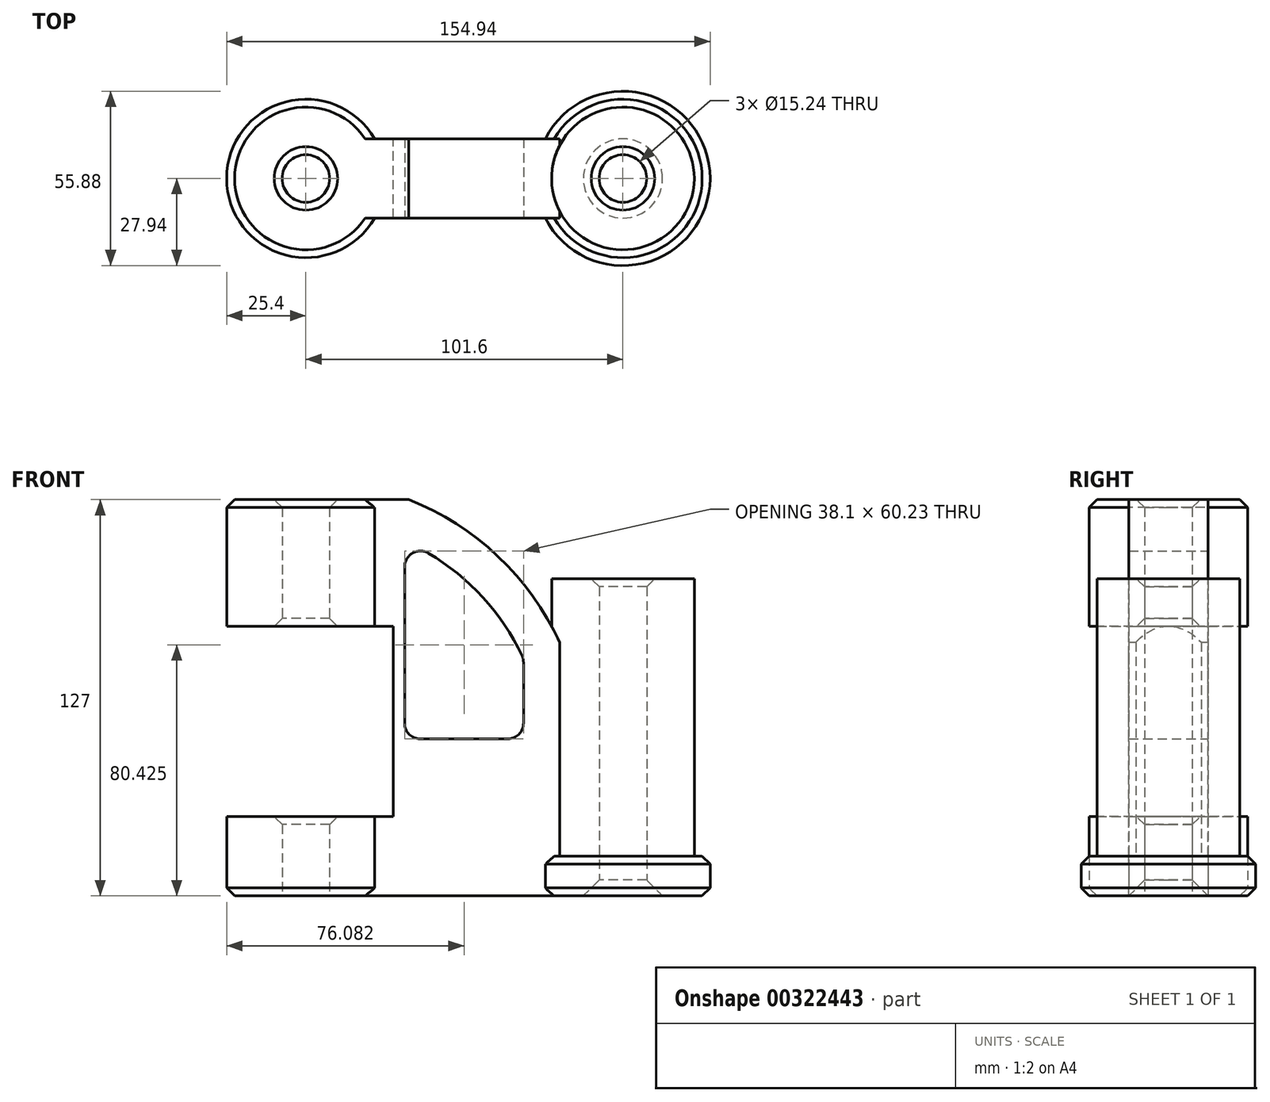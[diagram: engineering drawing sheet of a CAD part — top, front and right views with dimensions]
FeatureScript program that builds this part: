
annotation { "Feature Type Name" : "Feature", "Feature Type Description" : "" }
export const myFeature = defineFeature(function(context is Context, id is Id, definition is map)
    precondition{}
    {
        {
            var Q0;
            Q0=qCreatedBy(makeId("Top.planeOp"),FACE);
            var sketch = newSketch(context, id + "F0", { "sketchPlane" : qUnion([Q0])});
            skCircle(sketch, "E0", {"center": v(0, 0) * mm, "radius": 7.62 * mm});
            skCircle(sketch, "E1", {"center": v(0, 0) * mm, "radius": 25.4 * mm});
            skCircle(sketch, "E2", {"center": v(101.6, 0) * mm, "radius": 7.62 * mm});
            skCircle(sketch, "E3", {"center": v(101.6, 0) * mm, "radius": 22.86 * mm});
            skSolve(sketch);
        }
        {
            var Q0;
            Q0=makeQuery(id+"F0.imprint","IMPRINT",FACE,{"disambiguationData":[TD([[makeQuery(id+"F0.imprint","IMPRINT",EDGE,{"derivedFrom":sQuery(id+"F0.wireOp",EDGE,"E0")}),-1.0]])]});
            extrude(context, id + "F1", {"entities" : qUnion([Q0]), "depth" : 127 * mm});
        }
        {
            var Q0;
            Q0=makeQuery(id+"F0.imprint","IMPRINT",FACE,{"disambiguationData":[TD([[makeQuery(id+"F0.imprint","IMPRINT",EDGE,{"derivedFrom":sQuery(id+"F0.wireOp",EDGE,"E2")}),-1.0]])]});
            extrude(context, id + "F2", {"entities" : qUnion([Q0]), "depth" : 101.6 * mm});
        }
        {
            var Q0;
            Q0=qCreatedBy(makeId("Front.planeOp"),FACE);
            var sketch = newSketch(context, id + "F3", { "sketchPlane" : qUnion([Q0])});
            skLineSegment(sketch, "E4", {"start": v(20.32, 0) * mm, "end": v(20.32, 127) * mm});
            skLineSegment(sketch, "E5", {"start": v(20.32, 127) * mm, "end": v(33.02, 127) * mm});
            skLineSegment(sketch, "E6", {"start": v(20.32, 0) * mm, "end": v(81.28, 0) * mm});
            skLineSegment(sketch, "E7", {"start": v(81.28, 0) * mm, "end": v(81.28, 81.28) * mm});
            skArc(sketch, "E8", {"start": v(81.28, 81.28) * mm, "mid": v(61.58, 108.82) * mm, "end": v(33.02, 127) * mm});
            skArc(sketch, "E9.0", {"start": v(69.73, 76) * mm, "mid": v(54.12, 98.37) * mm, "end": v(31.63, 113.8) * mm});
            skLineSegment(sketch, "E10", {"start": v(31.63, 113.8) * mm, "end": v(31.63, 50.3) * mm});
            skLineSegment(sketch, "E11", {"start": v(31.63, 50.3) * mm, "end": v(69.73, 50.3) * mm});
            skLineSegment(sketch, "E12", {"start": v(69.73, 50.3) * mm, "end": v(69.73, 76) * mm});
            skSolve(sketch);
        }
        {
            var Q0;
            Q0 = qSketchRegion(id + "F3", true);
            extrude(context, id + "F4", {"entities" : qUnion([Q0]), "operationType" : NewBodyOperationType.ADD, "depth" : 25.4 * mm, "symmetric" : true});
        }
        {
            var Q0;
            Q0=qCreatedBy(makeId("Front.planeOp"),FACE);
            var sketch = newSketch(context, id + "F5", { "sketchPlane" : qUnion([Q0])});
            skLineSegment(sketch, "E13.bottom", {"start": v(-33.02, 25.4) * mm, "end": v(27.94, 25.4) * mm});
            skLineSegment(sketch, "E13.top", {"start": v(-33.02, 86.36) * mm, "end": v(27.94, 86.36) * mm});
            skLineSegment(sketch, "E13.left", {"start": v(-33.02, 25.4) * mm, "end": v(-33.02, 86.36) * mm});
            skLineSegment(sketch, "E13.right", {"start": v(27.94, 25.4) * mm, "end": v(27.94, 86.36) * mm});
            skSolve(sketch);
        }
        {
            var Q0;
            Q0 = qSketchRegion(id + "F5", true);
            extrude(context, id + "F6", {"entities" : qUnion([Q0]), "operationType" : NewBodyOperationType.REMOVE, "depth" : 101.6 * mm, "symmetric" : true});
        }
        {
            var Q0;
            Q0=makeQuery(id+"F4.opExtrude","SWEPT_EDGE",EDGE,{"disambiguationData":[OSD([sQuery(id+"F3.wireOp",EDGE,"E10"),sQuery(id+"F3.wireOp",EDGE,"E11")])]});
            var Q1;
            Q1=makeQuery(id+"F4.opExtrude","SWEPT_EDGE",EDGE,{"disambiguationData":[OSD([sQuery(id+"F3.wireOp",EDGE,"E9.0"),sQuery(id+"F3.wireOp",EDGE,"E10")])]});
            var Q2;
            Q2=makeQuery(id+"F4.opExtrude","SWEPT_EDGE",EDGE,{"disambiguationData":[OSD([sQuery(id+"F3.wireOp",EDGE,"E11"),sQuery(id+"F3.wireOp",EDGE,"E12")])]});
            var Q3;
            Q3=makeQuery(id+"F4.opExtrude","SWEPT_EDGE",EDGE,{"disambiguationData":[OSD([sQuery(id+"F3.wireOp",EDGE,"E9.0"),sQuery(id+"F3.wireOp",EDGE,"E12")])]});
            fillet(context, id + "F7", {"entities" : qUnion([Q0, Q1, Q2, Q3]), "radius" : 5.08 * mm, "tangentPropagation" : true, "allowEdgeOverflow" : false});
        }
        {
            var Q0;
            Q0=makeQuery(id+"F1.opExtrude","CAP_EDGE",EDGE,{"disambiguationData":[OSD([sQuery(id+"F0.wireOp",EDGE,"E1")])],"isStart":false});
            var Q1;
            Q1=makeQuery(id+"F1.opExtrude","CAP_EDGE",EDGE,{"disambiguationData":[OSD([sQuery(id+"F0.wireOp",EDGE,"E1")])],"isStart":true});
            var Q2;
            Q2=makeQuery(id+"F6.boolean.opBoolean","INTERSECT",EDGE,{"derivedFrom":[makeQuery(id+"F1.opExtrude","SWEPT_FACE",FACE,{"disambiguationData":[OSD([sQuery(id+"F0.wireOp",EDGE,"E0")])]}),makeQuery(id+"F6.opExtrude","SWEPT_FACE",FACE,{"disambiguationData":[OSD([sQuery(id+"F5.wireOp",EDGE,"E13.top")])]})]});
            var Q3;
            Q3=makeQuery(id+"F6.boolean.opBoolean","INTERSECT",EDGE,{"derivedFrom":[makeQuery(id+"F1.opExtrude","SWEPT_FACE",FACE,{"disambiguationData":[OSD([sQuery(id+"F0.wireOp",EDGE,"E0")])]}),makeQuery(id+"F6.opExtrude","SWEPT_FACE",FACE,{"disambiguationData":[OSD([sQuery(id+"F5.wireOp",EDGE,"E13.bottom")])]})]});
            chamfer(context, id + "F8", {"entities" : qUnion([Q0, Q1, Q2, Q3]), "width" : 2.54 * mm, "tangentPropagation" : true});
        }
        {
            var Q0;
            Q0=qCreatedBy(makeId("Top.planeOp"),FACE);
            var sketch = newSketch(context, id + "F9", { "sketchPlane" : qUnion([Q0])});
            skCircle(sketch, "E14.0", {"center": v(101.6, 0) * mm, "radius": 22.86 * mm});
            skCircle(sketch, "E15.0", {"center": v(101.6, 0) * mm, "radius": 27.94 * mm});
            skSolve(sketch);
        }
        {
            var Q0;
            Q0 = qSketchRegion(id + "F9", true);
            extrude(context, id + "F10", {"entities" : qUnion([Q0]), "operationType" : NewBodyOperationType.ADD, "depth" : 12.7 * mm});
        }
        {
            var Q0;
            Q0=makeQuery(id+"F2.opExtrude","CAP_EDGE",EDGE,{"disambiguationData":[OSD([sQuery(id+"F0.wireOp",EDGE,"E2")])],"isStart":true});
            chamfer(context, id + "F11", {"entities" : qUnion([Q0]), "width" : 5.08 * mm, "tangentPropagation" : true});
        }
        {
            var Q0;
            Q0=makeQuery(id+"F2.opExtrude","CAP_EDGE",EDGE,{"disambiguationData":[OSD([sQuery(id+"F0.wireOp",EDGE,"E2")])],"isStart":false});
            chamfer(context, id + "F12", {"entities" : qUnion([Q0]), "width" : 2.54 * mm, "tangentPropagation" : true});
        }
        {
            var Q0;
            Q0=makeQuery(id+"F10.opExtrude","CAP_EDGE",EDGE,{"disambiguationData":[OSD([sQuery(id+"F9.wireOp",EDGE,"E15.0")])],"isStart":false});
            var Q1;
            Q1=makeQuery(id+"F10.opExtrude","CAP_EDGE",EDGE,{"disambiguationData":[OSD([sQuery(id+"F9.wireOp",EDGE,"E15.0")])],"isStart":true});
            chamfer(context, id + "F13", {"entities" : qUnion([Q0, Q1]), "width" : 2.54 * mm, "tangentPropagation" : true});
        }
        {
            var Q0;
            Q0=makeQuery(id+"F1.opExtrude","CAP_EDGE",EDGE,{"disambiguationData":[OSD([sQuery(id+"F0.wireOp",EDGE,"E0")])],"isStart":false});
            chamfer(context, id + "F14", {"entities" : qUnion([Q0]), "width" : 2.54 * mm, "tangentPropagation" : true});
        }
    });
